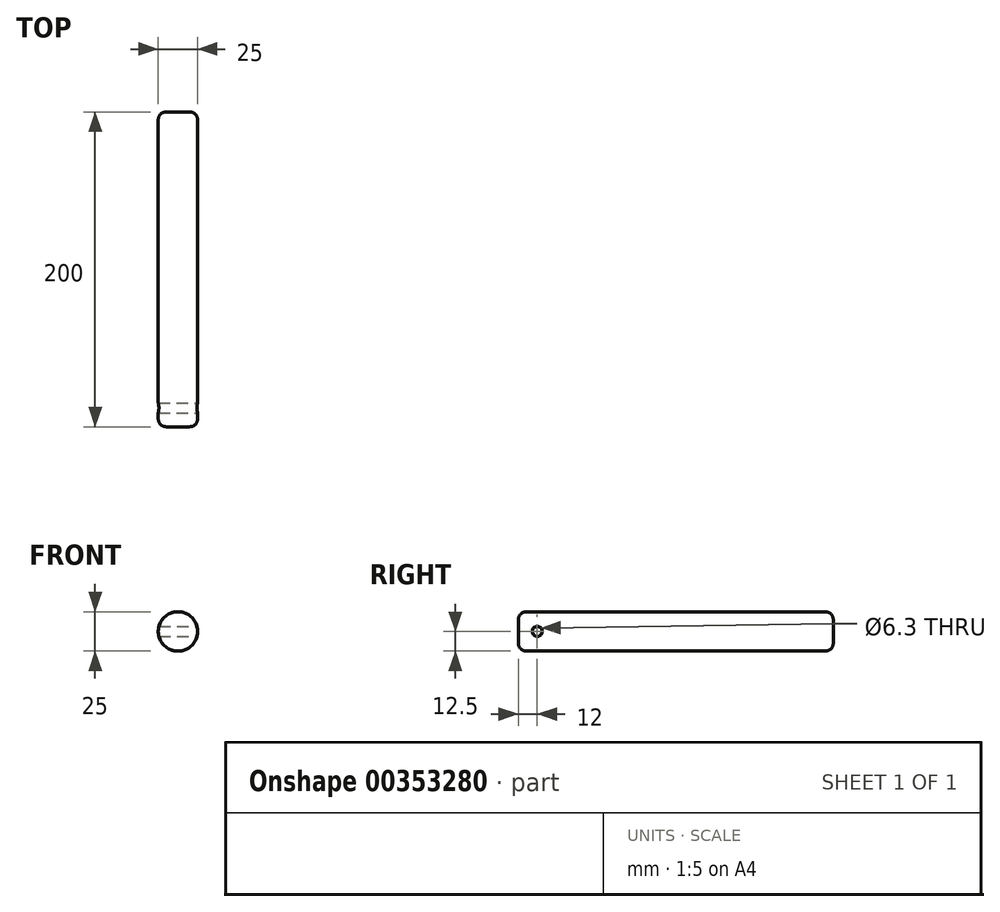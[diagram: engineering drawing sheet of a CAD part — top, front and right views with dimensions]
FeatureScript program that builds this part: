
annotation { "Feature Type Name" : "Feature", "Feature Type Description" : "" }
export const myFeature = defineFeature(function(context is Context, id is Id, definition is map)
    precondition{}
    {
        {
            var Q0;
            Q0=qCreatedBy(makeId("Front.planeOp"),FACE);
            var sketch = newSketch(context, id + "F0", { "sketchPlane" : qUnion([Q0])});
            skCircle(sketch, "E0", {"center": v(0, 0) * mm, "radius": 12.5 * mm});
            skSolve(sketch);
        }
        {
            var Q0;
            Q0=qCreatedBy(makeId("Right.planeOp"),FACE);
            var sketch = newSketch(context, id + "F1", { "sketchPlane" : qUnion([Q0])});
            skCircle(sketch, "E1", {"center": v(-88, 0) * mm, "radius": 3.15 * mm});
            skCircle(sketch, "E2.MirrorC", {"center": v(88, 0) * mm, "radius": 3.15 * mm});
            skLineSegment(sketch, "E3", {"start": v(-88, 0) * mm, "end": v(-76, 0) * mm});
            skSolve(sketch);
        }
        {
            var Q0;
            Q0=makeQuery(id+"F0.imprint","IMPRINT",FACE,{"disambiguationData":[TD([[makeQuery(id+"F0.imprint","IMPRINT",EDGE,{"derivedFrom":sQuery(id+"F0.wireOp",EDGE,"E0")}),1.0]])]});
            extrude(context, id + "F2", {"entities" : qUnion([Q0]), "endBound" : BoundingType.SYMMETRIC, "depth" : 200 * mm});
        }
        {
            var Q0;
            Q0=makeQuery(id+"F1.imprint","IMPRINT",FACE,{"disambiguationData":[TD([[makeQuery(id+"F1.imprint","IMPRINT",EDGE,{"derivedFrom":sQuery(id+"F1.wireOp",EDGE,"E1")}),1.0]])]});
            var Q1;
            Q1=makeQuery(id+"F1.imprint","IMPRINT",FACE,{"disambiguationData":[TD([[makeQuery(id+"F1.imprint","IMPRINT",EDGE,{"derivedFrom":sQuery(id+"F1.wireOp",EDGE,"E2.MirrorC")}),-1.0]])]});
            extrude(context, id + "F3", {"entities" : qUnion([Q0, Q1]), "operationType" : NewBodyOperationType.REMOVE, "endBound" : BoundingType.SYMMETRIC, "oppositeDirection" : true, "depth" : 400 * mm});
        }
        {
            var Q0;
            Q0=makeQuery(id+"F2.opExtrude","CAP_FACE",FACE,{"disambiguationData":[OSD([sQuery(id+"F0.wireOp",EDGE,"E0")])],"isStart":false});
            var Q1;
            Q1=makeQuery(id+"F2.opExtrude","CAP_FACE",FACE,{"disambiguationData":[OSD([sQuery(id+"F0.wireOp",EDGE,"E0")])],"isStart":true});
            fillet(context, id + "F4", {"entities" : qUnion([Q0, Q1]), "radius" : 5 * mm, "tangentPropagation" : true, "allowEdgeOverflow" : false});
        }
    });
